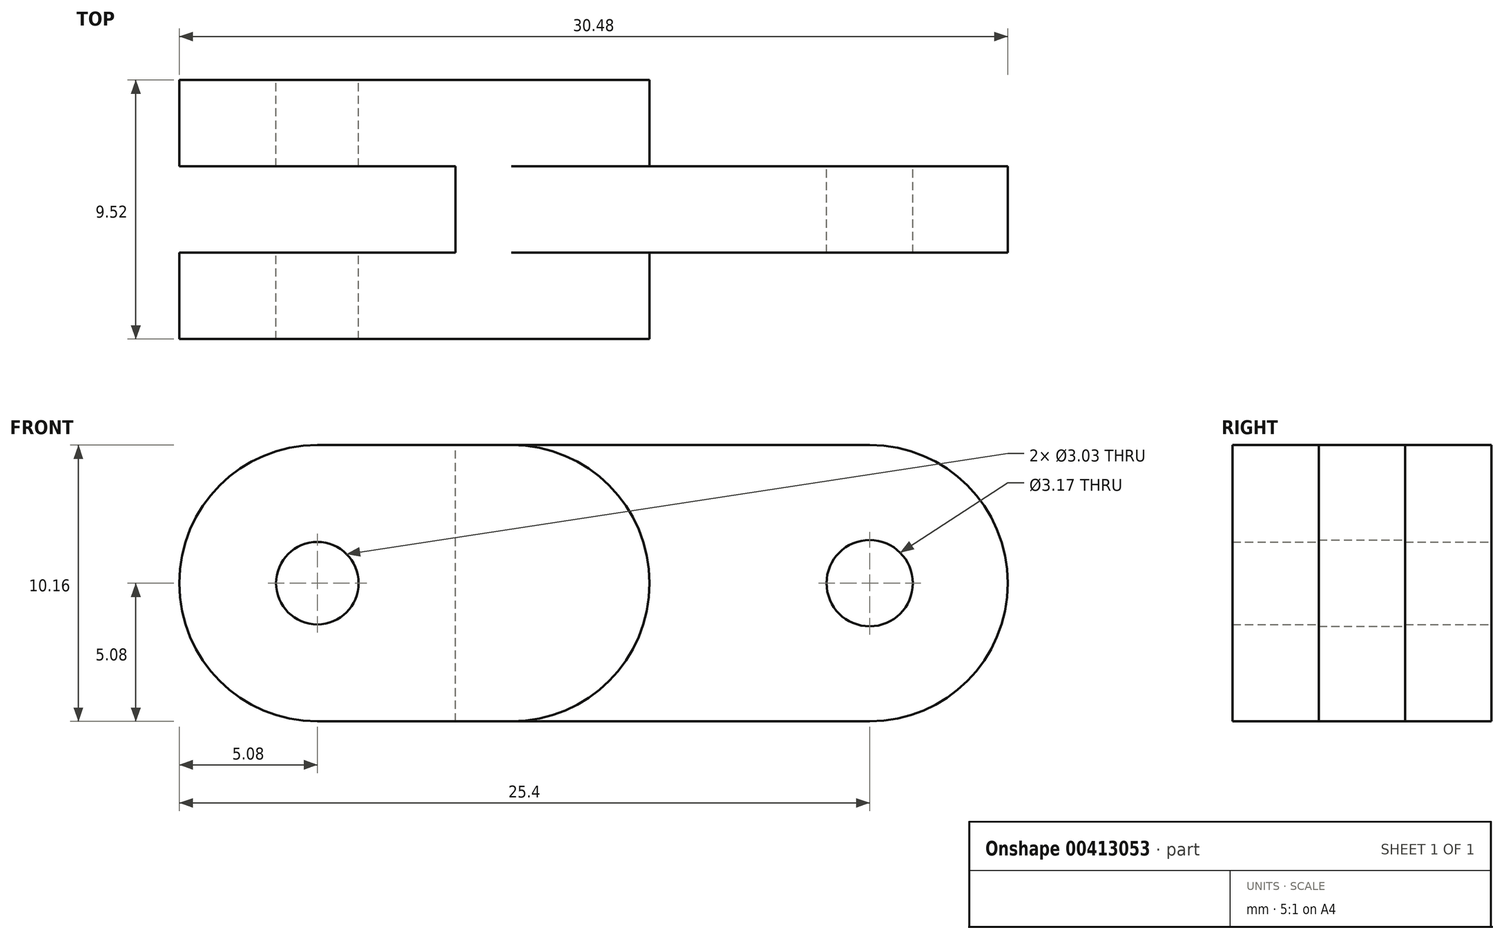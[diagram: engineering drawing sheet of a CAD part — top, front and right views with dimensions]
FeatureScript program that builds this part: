
annotation { "Feature Type Name" : "Feature", "Feature Type Description" : "" }
export const myFeature = defineFeature(function(context is Context, id is Id, definition is map)
    precondition{}
    {
        {
            var Q0;
            Q0=qCreatedBy(makeId("Front.planeOp"),FACE);
            var sketch = newSketch(context, id + "F0", { "sketchPlane" : qUnion([Q0])});
            skCircle(sketch, "E0", {"center": v(0, 0) * mm, "radius": 1.59 * mm});
            skCircle(sketch, "E1", {"center": v(20.32, 0) * mm, "radius": 1.59 * mm});
            skArc(sketch, "E2", {"start": v(0, 5.08) * mm, "mid": v(-5.08, 0) * mm, "end": v(0, -5.08) * mm});
            skArc(sketch, "E3", {"start": v(20.32, -5.08) * mm, "mid": v(25.4, 0) * mm, "end": v(20.32, 5.08) * mm});
            skLineSegment(sketch, "E4", {"start": v(0, 5.08) * mm, "end": v(20.32, 5.08) * mm});
            skLineSegment(sketch, "E5", {"start": v(0, -5.08) * mm, "end": v(20.32, -5.08) * mm});
            skSolve(sketch);
        }
        {
            var Q0;
            Q0 = qSketchRegion(id + "F0", true);
            extrude(context, id + "F1", {"entities" : qUnion([Q0]), "depth" : 1.59 * mm, "hasSecondDirection" : true, "secondDirectionOppositeDirection" : true, "secondDirectionDepth" : 1.59 * mm});
        }
        {
            var Q0;
            Q0=makeQuery(id+"F1.opExtrude","CAP_FACE",FACE,{"disambiguationData":[OSD([sQuery(id+"F0.wireOp",EDGE,"E0"),sQuery(id+"F0.wireOp",EDGE,"E1"),sQuery(id+"F0.wireOp",EDGE,"E2"),sQuery(id+"F0.wireOp",EDGE,"E3"),sQuery(id+"F0.wireOp",EDGE,"E4"),sQuery(id+"F0.wireOp",EDGE,"E5")])],"isStart":false});
            var sketch = newSketch(context, id + "F2", { "sketchPlane" : qUnion([Q0])});
            skArc(sketch, "E6", {"start": v(0, 5.08) * mm, "mid": v(-5.08, 0) * mm, "end": v(0, -5.08) * mm});
            skCircle(sketch, "E7", {"center": v(0, 0) * mm, "radius": 1.52 * mm});
            skArc(sketch, "E8", {"start": v(7.14, -5.08) * mm, "mid": v(12.22, 0) * mm, "end": v(7.14, 5.08) * mm});
            skLineSegment(sketch, "E9", {"start": v(7.14, 5.08) * mm, "end": v(0, 5.08) * mm});
            skLineSegment(sketch, "E10", {"start": v(0, -5.08) * mm, "end": v(7.14, -5.08) * mm});
            skSolve(sketch);
        }
        {
            var Q0;
            Q0 = qSketchRegion(id + "F2", true);
            extrude(context, id + "F3", {"entities" : qUnion([Q0]), "operationType" : NewBodyOperationType.ADD, "depth" : 3.17 * mm, "hasSecondDirection" : true, "secondDirectionOppositeDirection" : true, "secondDirectionDepth" : 6.35 * mm});
        }
        {
            var Q0;
            Q0=makeQuery(id+"F1.opExtrude","CAP_FACE",FACE,{"disambiguationData":[OSD([sQuery(id+"F0.wireOp",EDGE,"E0"),sQuery(id+"F0.wireOp",EDGE,"E1"),sQuery(id+"F0.wireOp",EDGE,"E2"),sQuery(id+"F0.wireOp",EDGE,"E3"),sQuery(id+"F0.wireOp",EDGE,"E4"),sQuery(id+"F0.wireOp",EDGE,"E5")])],"isStart":false});
            var sketch = newSketch(context, id + "F4", { "sketchPlane" : qUnion([Q0])});
            skLineSegment(sketch, "E11.bottom", {"start": v(5.08, -5.08) * mm, "end": v(-6.35, -5.08) * mm});
            skLineSegment(sketch, "E11.top", {"start": v(5.08, 5.08) * mm, "end": v(-6.35, 5.08) * mm});
            skLineSegment(sketch, "E11.left", {"start": v(5.08, -5.08) * mm, "end": v(5.08, 5.08) * mm});
            skLineSegment(sketch, "E11.right", {"start": v(-6.35, -5.08) * mm, "end": v(-6.35, 5.08) * mm});
            skSolve(sketch);
        }
        {
            var Q0;
            Q0 = qSketchRegion(id + "F4", true);
            extrude(context, id + "F5", {"entities" : qUnion([Q0]), "operationType" : NewBodyOperationType.REMOVE, "oppositeDirection" : true, "depth" : 3.17 * mm});
        }
    });
